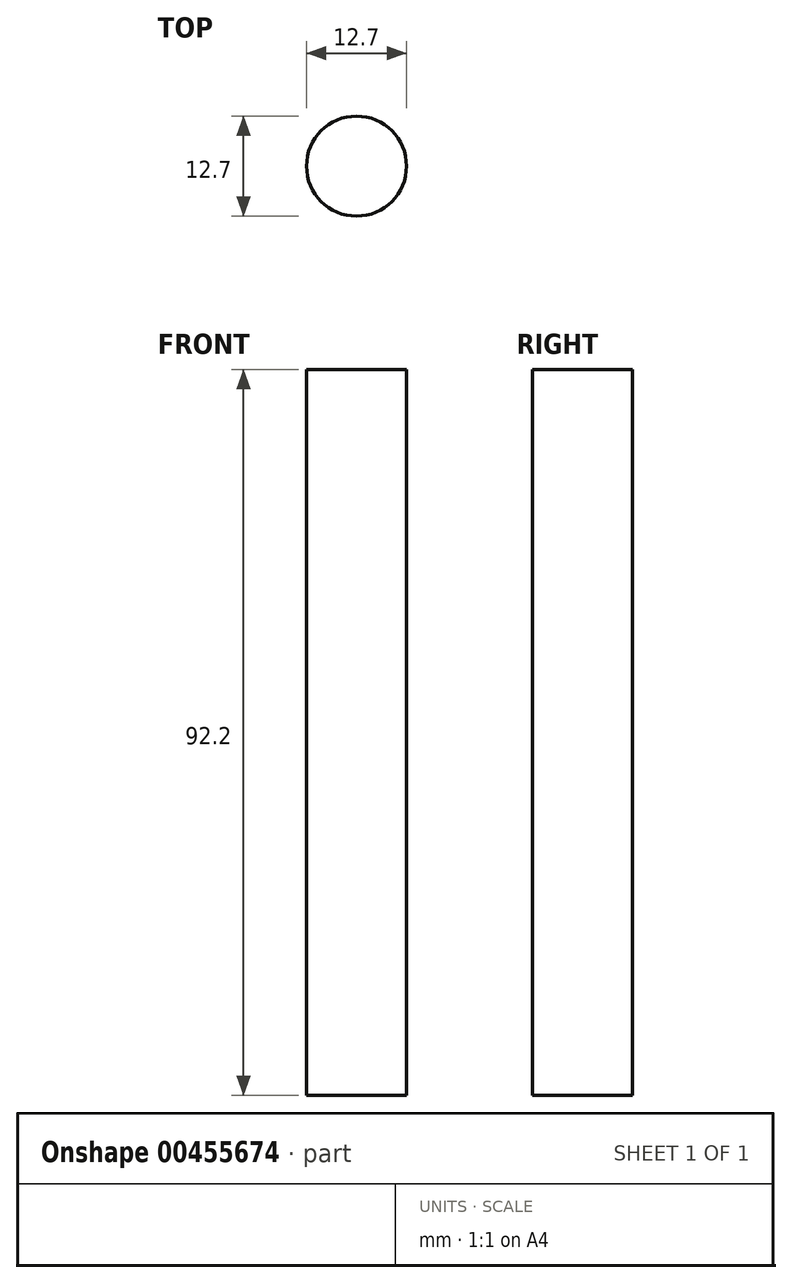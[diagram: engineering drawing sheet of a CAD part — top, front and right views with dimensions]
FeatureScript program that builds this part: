
annotation { "Feature Type Name" : "Feature", "Feature Type Description" : "" }
export const myFeature = defineFeature(function(context is Context, id is Id, definition is map)
    precondition{}
    {
        {
            var Q0;
            Q0=qCreatedBy(makeId("Top.planeOp"),FACE);
            var sketch = newSketch(context, id + "F0", { "sketchPlane" : qUnion([Q0])});
            skCircle(sketch, "E0", {"center": v(0, 0) * mm, "radius": 6.35 * mm});
            skSolve(sketch);
        }
        {
            var Q0;
            Q0 = qSketchRegion(id + "F0", true);
            extrude(context, id + "F1", {"entities" : qUnion([Q0]), "depth" : 92.2 * mm, "offsetDistance" : 25.4 * mm});
        }
    });
